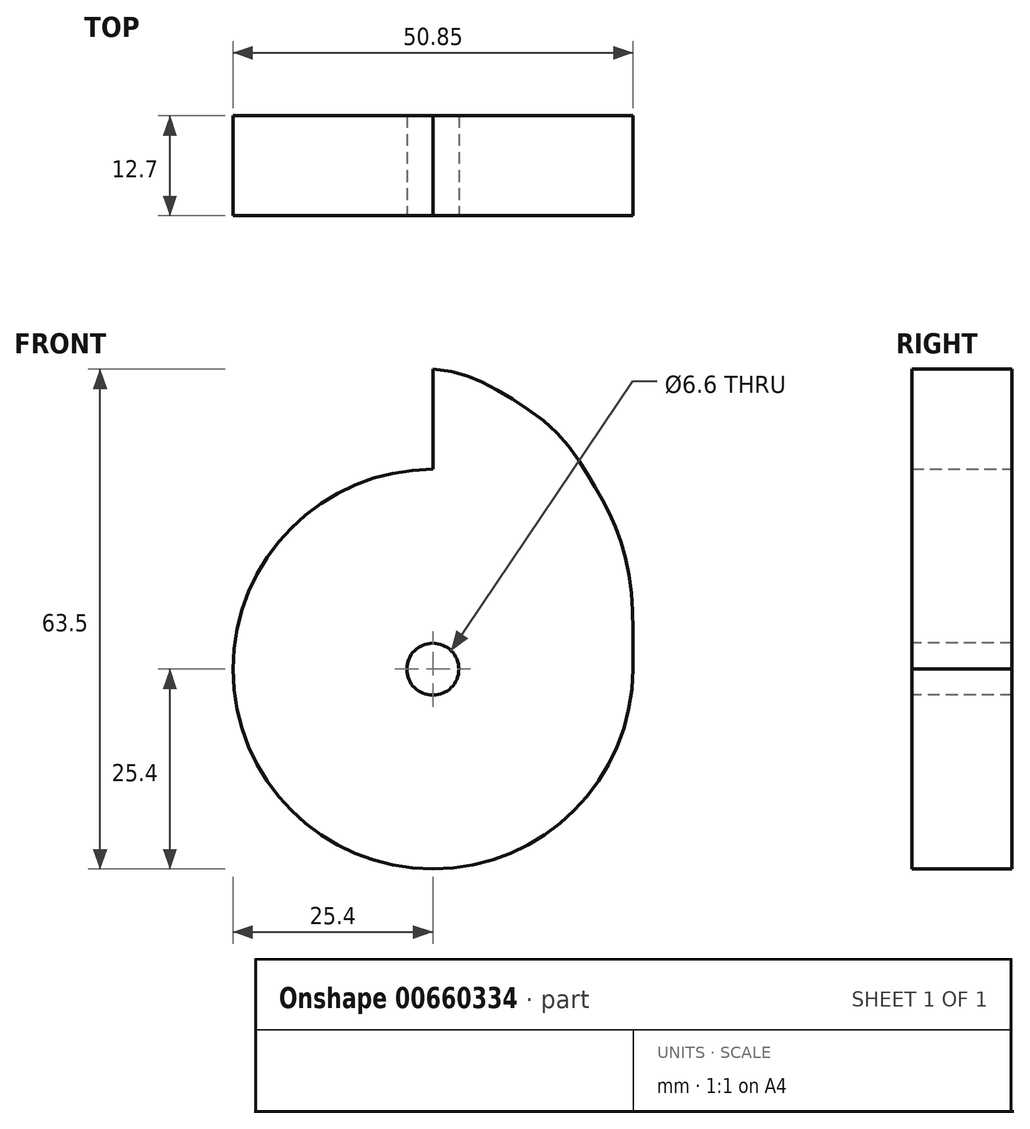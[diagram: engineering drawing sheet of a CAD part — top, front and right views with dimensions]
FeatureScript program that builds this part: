
annotation { "Feature Type Name" : "Feature", "Feature Type Description" : "" }
export const myFeature = defineFeature(function(context is Context, id is Id, definition is map)
    precondition{}
    {
        {
            var Q0;
            Q0=qCreatedBy(makeId("Front.planeOp"),FACE);
            var sketch = newSketch(context, id + "F0", { "sketchPlane" : qUnion([Q0])});
            skCircle(sketch, "E0", {"center": v(0, 0) * mm, "radius": 25.4 * mm});
            skLineSegment(sketch, "E1", {"start": v(0, 25.4) * mm, "end": v(0, 38.1) * mm});
            skFitSpline(sketch, "E2", {"points": [v(0, 38.1) * mm, v(7.67, 35.72) * mm, v(15.59, 30.2) * mm, v(20.24, 23.79) * mm, v(23.2, 18.07) * mm, v(25.14, 10.3) * mm, v(25.4, 0) * mm], "startDerivative": vector(60.76, -3.08) * mm, "endDerivative": vector(-1.19, -58.53) * mm});
            skSolve(sketch);
        }
        {
            var Q0;
            {var subQ0=sQuery(id+"F0.wireOp",EDGE,"E0");var subQ1=makeQuery(id+"F0.imprint","INTERSECT",VERTEX,{"derivedFrom":[subQ0,sQuery(id+"F0.wireOp",EDGE,"E1")]});Q0=makeQuery(id+"F0.imprint","IMPRINT",FACE,{"disambiguationData":[TD([[makeQuery(id+"F0.imprint","IMPRINT",EDGE,{"disambiguationData":[TD([[subQ1,1.0]])],"derivedFrom":subQ0}),1.0]])]});}
            extrude(context, id + "F1", {"entities" : qUnion([Q0]), "depth" : 12.7 * mm, "offsetDistance" : 25.4 * mm});
        }
        {
            var Q0;
            Q0 = qSketchRegion(id + "F0", true);
            extrude(context, id + "F2", {"entities" : qUnion([Q0]), "operationType" : NewBodyOperationType.ADD, "depth" : 12.7 * mm, "offsetDistance" : 25.4 * mm});
        }
        {
            var Q0;
            {var subQ0=sQuery(id+"F0.wireOp",EDGE,"E0");Q0=makeQuery(id+"F2.boolean.opBoolean","MERGE",FACE,{"derivedFrom":[makeQuery(id+"F1.opExtrude","CAP_FACE",FACE,{"disambiguationData":[OSD([subQ0])],"isStart":false}),makeQuery(id+"F2.opExtrude","CAP_FACE",FACE,{"disambiguationData":[OSD([subQ0,sQuery(id+"F0.wireOp",EDGE,"E1"),sQuery(id+"F0.wireOp",EDGE,"E2")])],"isStart":false})]});}
            var sketch = newSketch(context, id + "F3", { "sketchPlane" : qUnion([Q0])});
            skCircle(sketch, "E3", {"center": v(0, 0) * mm, "radius": 3.3 * mm});
            skSolve(sketch);
        }
        {
            var Q0;
            Q0=makeQuery(id+"F3.imprint","IMPRINT",FACE,{"disambiguationData":[TD([[makeQuery(id+"F3.imprint","IMPRINT",EDGE,{"derivedFrom":sQuery(id+"F3.wireOp",EDGE,"E3")}),1.0]])]});
            extrude(context, id + "F4", {"entities" : qUnion([Q0]), "operationType" : NewBodyOperationType.REMOVE, "oppositeDirection" : true, "depth" : 41.15 * mm, "offsetDistance" : 25.4 * mm});
        }
    });
